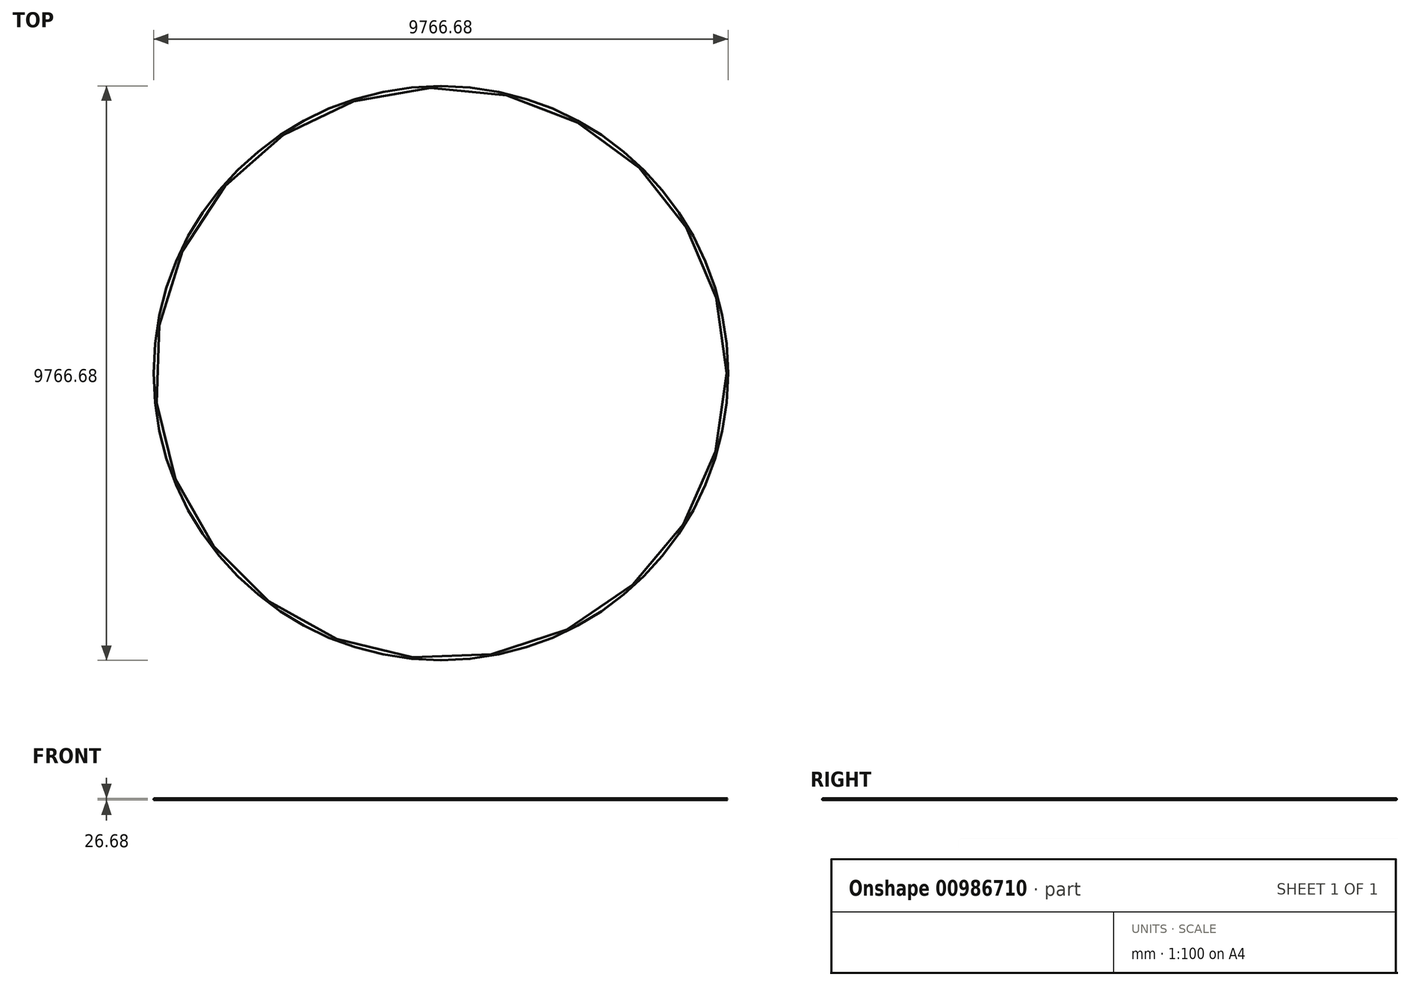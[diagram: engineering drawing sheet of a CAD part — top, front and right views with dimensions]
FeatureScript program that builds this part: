
annotation { "Feature Type Name" : "Feature", "Feature Type Description" : "" }
export const myFeature = defineFeature(function(context is Context, id is Id, definition is map)
    precondition{}
    {
        {
            var Q0;
            Q0=qCreatedBy(makeId("Front.planeOp"),FACE);
            var sketch = newSketch(context, id + "F0", { "sketchPlane" : qUnion([Q0])});
            skCircle(sketch, "E0", {"center": v(0, 0) * mm, "radius": 13.34 * mm});
            skCircle(sketch, "E1.0", {"center": v(0, 0) * mm, "radius": 11.23 * mm});
            skLineSegment(sketch, "E2", {"start": v(0, 0) * mm, "end": v(4870, 0) * mm, "construction": true});
            skLineSegment(sketch, "E3", {"start": v(4870, 0) * mm, "end": v(4870, -100) * mm, "construction": true});
            skSolve(sketch);
        }
        {
            var Q0;
            Q0 = qSketchRegion(id + "F0", true);
            var Q1;
            Q1=sQuery(id+"F0.wireOp",EDGE,"E3");
            revolve(context, id + "F1", {"surfaceOperationType" : NewSurfaceOperationType.NEW, "entities" : qUnion([Q0]), "axis" : qUnion([Q1]), "revolveType" : RevolveType.FULL});
        }
    });
